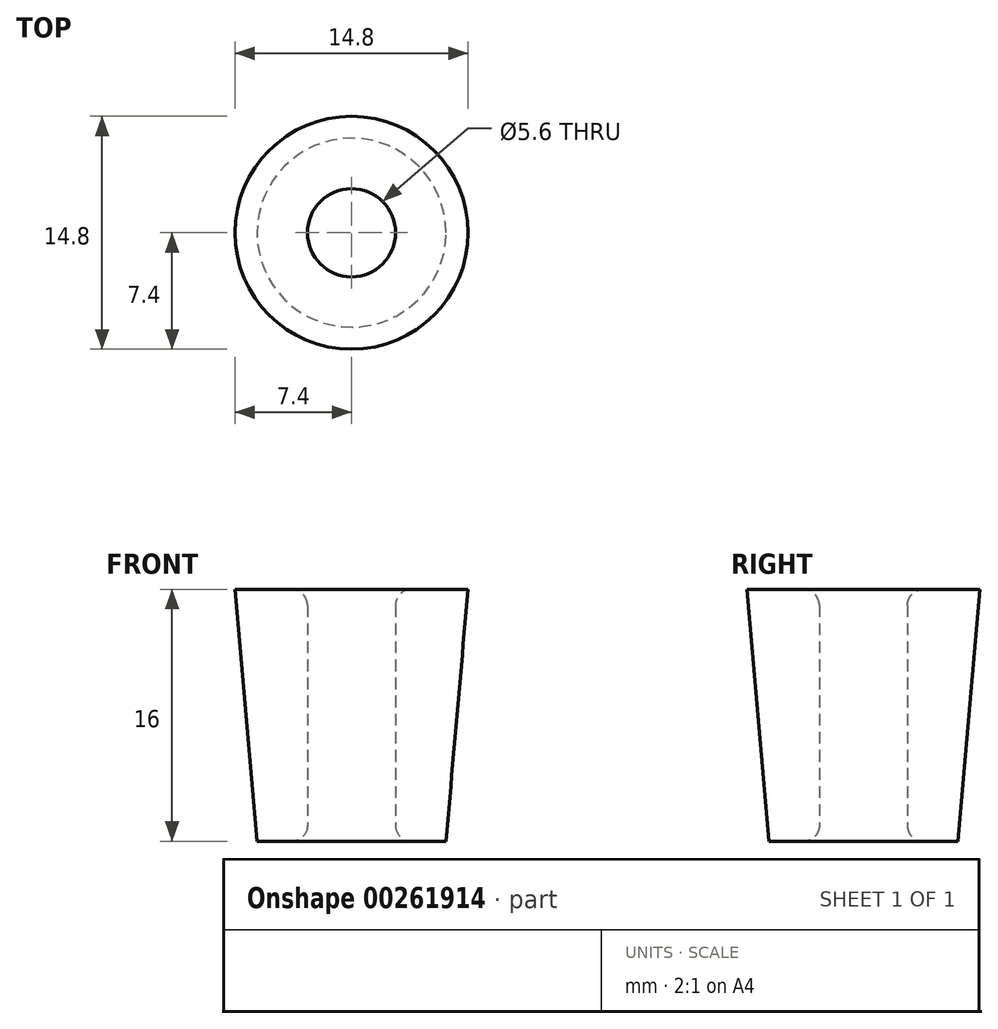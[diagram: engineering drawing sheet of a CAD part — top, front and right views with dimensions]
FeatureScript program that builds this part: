
annotation { "Feature Type Name" : "Feature", "Feature Type Description" : "" }
export const myFeature = defineFeature(function(context is Context, id is Id, definition is map)
    precondition{}
    {
        {
            var Q0;
            Q0=qCreatedBy(makeId("Top.planeOp"),FACE);
            var sketch = newSketch(context, id + "F0", { "sketchPlane" : qUnion([Q0])});
            skCircle(sketch, "E0", {"center": v(0, 0) * mm, "radius": 2.8 * mm});
            skCircle(sketch, "E1", {"center": v(0, 0) * mm, "radius": 6 * mm});
            skSolve(sketch);
        }
        {
            var Q0;
            Q0=makeQuery(id+"F0.imprint","IMPRINT",FACE,{"disambiguationData":[TD([[makeQuery(id+"F0.imprint","IMPRINT",EDGE,{"derivedFrom":sQuery(id+"F0.wireOp",EDGE,"E0")}),-1.0]])]});
            extrude(context, id + "F1", {"entities" : qUnion([Q0]), "depth" : 16 * mm, "hasDraft" : true, "draftAngle" : 5 * degree});
        }
        {
            var Q0;
            Q0=makeQuery(id+"F0.imprint","IMPRINT",FACE,{"disambiguationData":[TD([[makeQuery(id+"F0.imprint","IMPRINT",EDGE,{"derivedFrom":sQuery(id+"F0.wireOp",EDGE,"E0")}),1.0]])]});
            extrude(context, id + "F2", {"entities" : qUnion([Q0]), "operationType" : NewBodyOperationType.REMOVE, "endBound" : BoundingType.THROUGH_ALL, "depth" : 25 * mm});
        }
        {
            var Q0;
            {var subQ0=sQuery(id+"F0.wireOp",EDGE,"E0");Q0=makeQuery(id+"F2.boolean.opBoolean","INTERSECT",EDGE,{"derivedFrom":[makeQuery(id+"F1.opExtrude","CAP_FACE",FACE,{"disambiguationData":[OSD([subQ0,sQuery(id+"F0.wireOp",EDGE,"E1")])],"isStart":false}),makeQuery(id+"F2.opExtrude","SWEPT_FACE",FACE,{"disambiguationData":[OSD([subQ0])]})]});}
            var Q1;
            {var subQ0=sQuery(id+"F0.wireOp",EDGE,"E0");Q1=makeQuery(id+"F2.boolean.opBoolean","MERGE",EDGE,{"derivedFrom":[makeQuery(id+"F1.opExtrude","CAP_EDGE",EDGE,{"disambiguationData":[OSD([subQ0])],"isStart":true}),makeQuery(id+"F2.opExtrude","CAP_EDGE",EDGE,{"disambiguationData":[OSD([subQ0])],"isStart":true})]});}
            fillet(context, id + "F3", {"entities" : qUnion([Q0, Q1]), "radius" : 1 * mm, "tangentPropagation" : true, "allowEdgeOverflow" : false});
        }
        {
            var Q0;
            Q0=qCreatedBy(makeId("Top.planeOp"),FACE);
            cPlane(context, id + "F4", {"entities" : qUnion([Q0]), "cplaneType" : CPlaneType.OFFSET, "offset" : 15 * mm, "width" : 150 * mm, "height" : 150 * mm});
        }
    });
